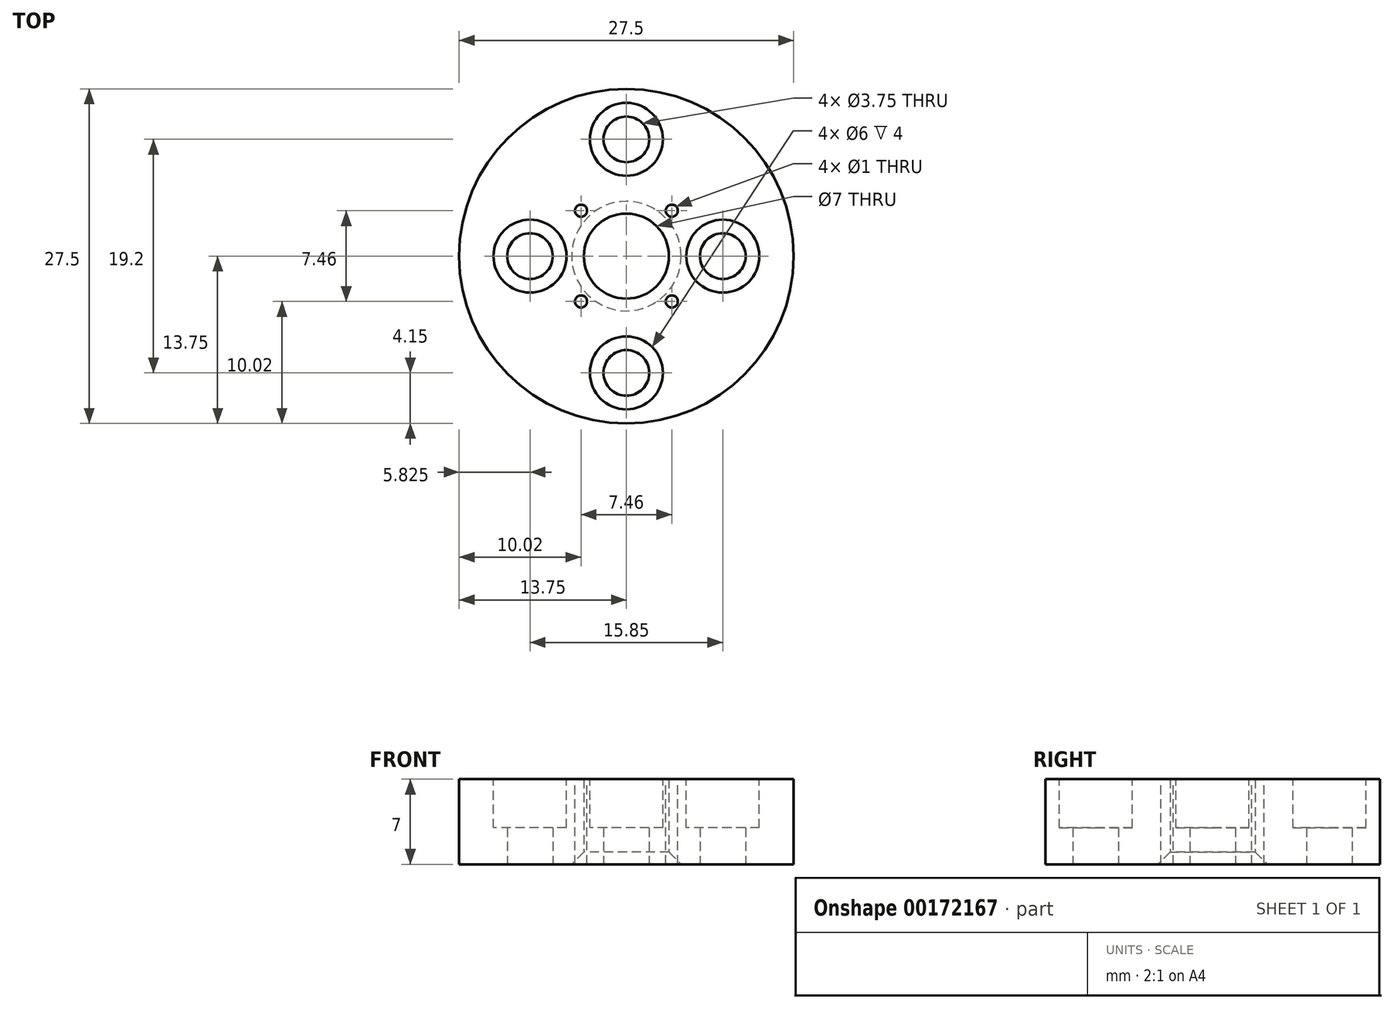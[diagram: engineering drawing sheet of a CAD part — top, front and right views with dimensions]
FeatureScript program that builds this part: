
annotation { "Feature Type Name" : "Feature", "Feature Type Description" : "" }
export const myFeature = defineFeature(function(context is Context, id is Id, definition is map)
    precondition{}
    {
        {
            var Q0;
            Q0=qCreatedBy(makeId("Top.planeOp"),FACE);
            var sketch = newSketch(context, id + "F0", { "sketchPlane" : qUnion([Q0])});
            skCircle(sketch, "E0", {"center": v(0, 0) * mm, "radius": 13.75 * mm});
            skCircle(sketch, "E1", {"center": v(0, 0) * mm, "radius": 3.5 * mm});
            skCircle(sketch, "E2", {"center": v(0, 0) * mm, "radius": 7.92 * mm, "construction": true});
            skCircle(sketch, "E3", {"center": v(0, 0) * mm, "radius": 9.6 * mm, "construction": true});
            skLineSegment(sketch, "E4", {"start": v(-23.13, 0) * mm, "end": v(27.16, 0) * mm, "construction": true});
            skLineSegment(sketch, "E5", {"start": v(0, 22.98) * mm, "end": v(0, -19.77) * mm, "construction": true});
            skCircle(sketch, "E6", {"center": v(0, 9.6) * mm, "radius": 1.88 * mm});
            skCircle(sketch, "E7", {"center": v(0, -9.6) * mm, "radius": 1.88 * mm});
            skCircle(sketch, "E8", {"center": v(7.92, 0) * mm, "radius": 1.88 * mm});
            skCircle(sketch, "E9", {"center": v(-7.92, 0) * mm, "radius": 1.88 * mm});
            skSolve(sketch);
        }
        {
            var Q0;
            Q0=makeQuery(id+"F0.imprint","IMPRINT",FACE,{"disambiguationData":[TD([[makeQuery(id+"F0.imprint","IMPRINT",EDGE,{"derivedFrom":sQuery(id+"F0.wireOp",EDGE,"E0")}),1.0]])]});
            extrude(context, id + "F1", {"entities" : qUnion([Q0]), "depth" : 7 * mm});
        }
        {
            var Q0;
            Q0=makeQuery(id+"F1.opExtrude","CAP_FACE",FACE,{"disambiguationData":[OSD([sQuery(id+"F0.wireOp",EDGE,"E0"),sQuery(id+"F0.wireOp",EDGE,"E1"),sQuery(id+"F0.wireOp",EDGE,"E6"),sQuery(id+"F0.wireOp",EDGE,"E7"),sQuery(id+"F0.wireOp",EDGE,"E8"),sQuery(id+"F0.wireOp",EDGE,"E9")])],"isStart":false});
            var sketch = newSketch(context, id + "F2", { "sketchPlane" : qUnion([Q0])});
            skCircle(sketch, "E10", {"center": v(0, 9.6) * mm, "radius": 3 * mm});
            skCircle(sketch, "E11", {"center": v(7.92, 0) * mm, "radius": 3 * mm});
            skCircle(sketch, "E12", {"center": v(0, -9.6) * mm, "radius": 3 * mm});
            skCircle(sketch, "E13", {"center": v(-7.92, 0) * mm, "radius": 3 * mm});
            skSolve(sketch);
        }
        {
            var Q0;
            Q0=makeQuery(id+"F2.imprint","IMPRINT",FACE,{"disambiguationData":[TD([[makeQuery(id+"F2.imprint","IMPRINT",EDGE,{"derivedFrom":sQuery(id+"F2.wireOp",EDGE,"E10")}),1.0]])]});
            var Q1;
            Q1=makeQuery(id+"F2.imprint","IMPRINT",FACE,{"disambiguationData":[TD([[makeQuery(id+"F2.imprint","IMPRINT",EDGE,{"derivedFrom":sQuery(id+"F2.wireOp",EDGE,"E13")}),1.0]])]});
            var Q2;
            Q2=makeQuery(id+"F2.imprint","IMPRINT",FACE,{"disambiguationData":[TD([[makeQuery(id+"F2.imprint","IMPRINT",EDGE,{"derivedFrom":sQuery(id+"F2.wireOp",EDGE,"E11")}),1.0]])]});
            var Q3;
            Q3=makeQuery(id+"F2.imprint","IMPRINT",FACE,{"disambiguationData":[TD([[makeQuery(id+"F2.imprint","IMPRINT",EDGE,{"derivedFrom":sQuery(id+"F2.wireOp",EDGE,"E12")}),1.0]])]});
            extrude(context, id + "F3", {"entities" : qUnion([Q0, Q1, Q2, Q3]), "operationType" : NewBodyOperationType.REMOVE, "oppositeDirection" : true, "depth" : 4 * mm});
        }
        {
            var Q0;
            Q0=makeQuery(id+"F1.opExtrude","CAP_FACE",FACE,{"disambiguationData":[OSD([sQuery(id+"F0.wireOp",EDGE,"E0"),sQuery(id+"F0.wireOp",EDGE,"E1"),sQuery(id+"F0.wireOp",EDGE,"E6"),sQuery(id+"F0.wireOp",EDGE,"E7"),sQuery(id+"F0.wireOp",EDGE,"E8"),sQuery(id+"F0.wireOp",EDGE,"E9")])],"isStart":false});
            var sketch = newSketch(context, id + "F4", { "sketchPlane" : qUnion([Q0])});
            skLineSegment(sketch, "E14", {"start": v(-9.34, 9.34) * mm, "end": v(8.33, -8.33) * mm, "construction": true});
            skLineSegment(sketch, "E15", {"start": v(9.7, 9.7) * mm, "end": v(-10, -10) * mm, "construction": true});
            skCircle(sketch, "E16", {"center": v(0, 0) * mm, "radius": 5.28 * mm, "construction": true});
            skCircle(sketch, "E17", {"center": v(3.73, 3.73) * mm, "radius": 0.5 * mm});
            skCircle(sketch, "E18", {"center": v(-3.73, 3.73) * mm, "radius": 0.5 * mm});
            skCircle(sketch, "E19", {"center": v(3.73, -3.73) * mm, "radius": 0.5 * mm});
            skCircle(sketch, "E20", {"center": v(-3.73, -3.73) * mm, "radius": 0.5 * mm});
            skSolve(sketch);
        }
        {
            var Q0;
            Q0=makeQuery(id+"F4.imprint","IMPRINT",FACE,{"disambiguationData":[TD([[makeQuery(id+"F4.imprint","IMPRINT",EDGE,{"derivedFrom":sQuery(id+"F4.wireOp",EDGE,"E18")}),1.0]])]});
            var Q1;
            Q1=makeQuery(id+"F4.imprint","IMPRINT",FACE,{"disambiguationData":[TD([[makeQuery(id+"F4.imprint","IMPRINT",EDGE,{"derivedFrom":sQuery(id+"F4.wireOp",EDGE,"E17")}),1.0]])]});
            var Q2;
            Q2=makeQuery(id+"F4.imprint","IMPRINT",FACE,{"disambiguationData":[TD([[makeQuery(id+"F4.imprint","IMPRINT",EDGE,{"derivedFrom":sQuery(id+"F4.wireOp",EDGE,"E19")}),1.0]])]});
            var Q3;
            Q3=makeQuery(id+"F4.imprint","IMPRINT",FACE,{"disambiguationData":[TD([[makeQuery(id+"F4.imprint","IMPRINT",EDGE,{"derivedFrom":sQuery(id+"F4.wireOp",EDGE,"E20")}),1.0]])]});
            extrude(context, id + "F5", {"entities" : qUnion([Q0, Q1, Q2, Q3]), "operationType" : NewBodyOperationType.REMOVE, "oppositeDirection" : true, "depth" : 8 * mm});
        }
        {
            var Q0;
            Q0=makeQuery(id+"F1.opExtrude","CAP_EDGE",EDGE,{"disambiguationData":[OSD([sQuery(id+"F0.wireOp",EDGE,"E1")])],"isStart":true});
            chamfer(context, id + "F6", {"entities" : qUnion([Q0]), "width" : 1 * mm, "tangentPropagation" : true});
        }
    });
